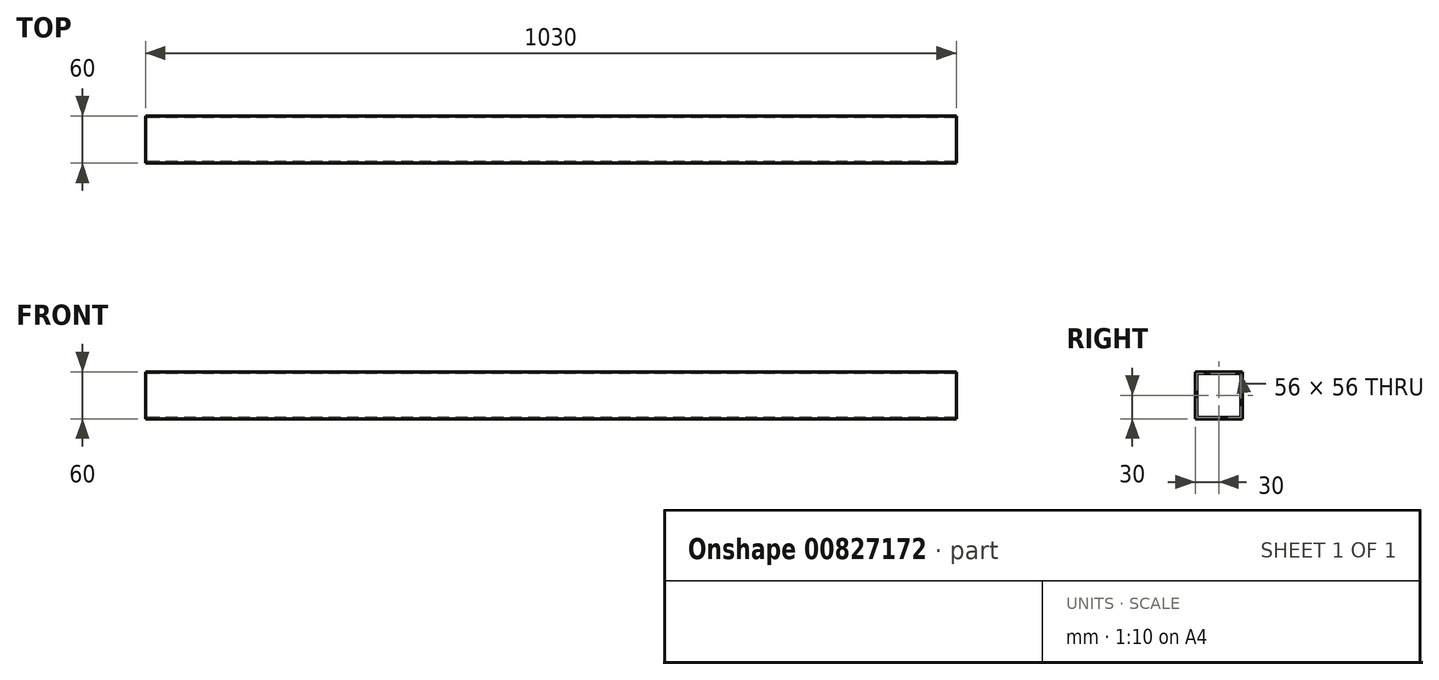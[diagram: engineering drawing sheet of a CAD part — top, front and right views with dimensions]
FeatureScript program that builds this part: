
annotation { "Feature Type Name" : "Feature", "Feature Type Description" : "" }
export const myFeature = defineFeature(function(context is Context, id is Id, definition is map)
    precondition{}
    {
        {
            var Q0;
            Q0=qCreatedBy(makeId("Right.planeOp"),FACE);
            var sketch = newSketch(context, id + "F0", { "sketchPlane" : qUnion([Q0])});
            skLineSegment(sketch, "E0.bottom", {"start": v(30, 30) * mm, "end": v(-30, 30) * mm});
            skLineSegment(sketch, "E0.top", {"start": v(30, -30) * mm, "end": v(-30, -30) * mm});
            skLineSegment(sketch, "E0.left", {"start": v(30, 30) * mm, "end": v(30, -30) * mm});
            skLineSegment(sketch, "E0.right", {"start": v(-30, 30) * mm, "end": v(-30, -30) * mm});
            skPoint(sketch, "E0.middle", {"position": v(0, 0) * mm});
            skLineSegment(sketch, "E1.bottom", {"start": v(28, 28) * mm, "end": v(-28, 28) * mm});
            skLineSegment(sketch, "E1.top", {"start": v(28, -28) * mm, "end": v(-28, -28) * mm});
            skLineSegment(sketch, "E1.left", {"start": v(28, 28) * mm, "end": v(28, -28) * mm});
            skLineSegment(sketch, "E1.right", {"start": v(-28, 28) * mm, "end": v(-28, -28) * mm});
            skSolve(sketch);
        }
        {
            var Q0;
            Q0=makeQuery(id+"F0.imprint","IMPRINT",FACE,{"disambiguationData":[TD([[makeQuery(id+"F0.imprint","IMPRINT",EDGE,{"derivedFrom":sQuery(id+"F0.wireOp",EDGE,"E0.bottom")}),1.0]])]});
            extrude(context, id + "F1", {"entities" : qUnion([Q0]), "depth" : 1030 * mm, "offsetDistance" : 25 * mm});
        }
    });
